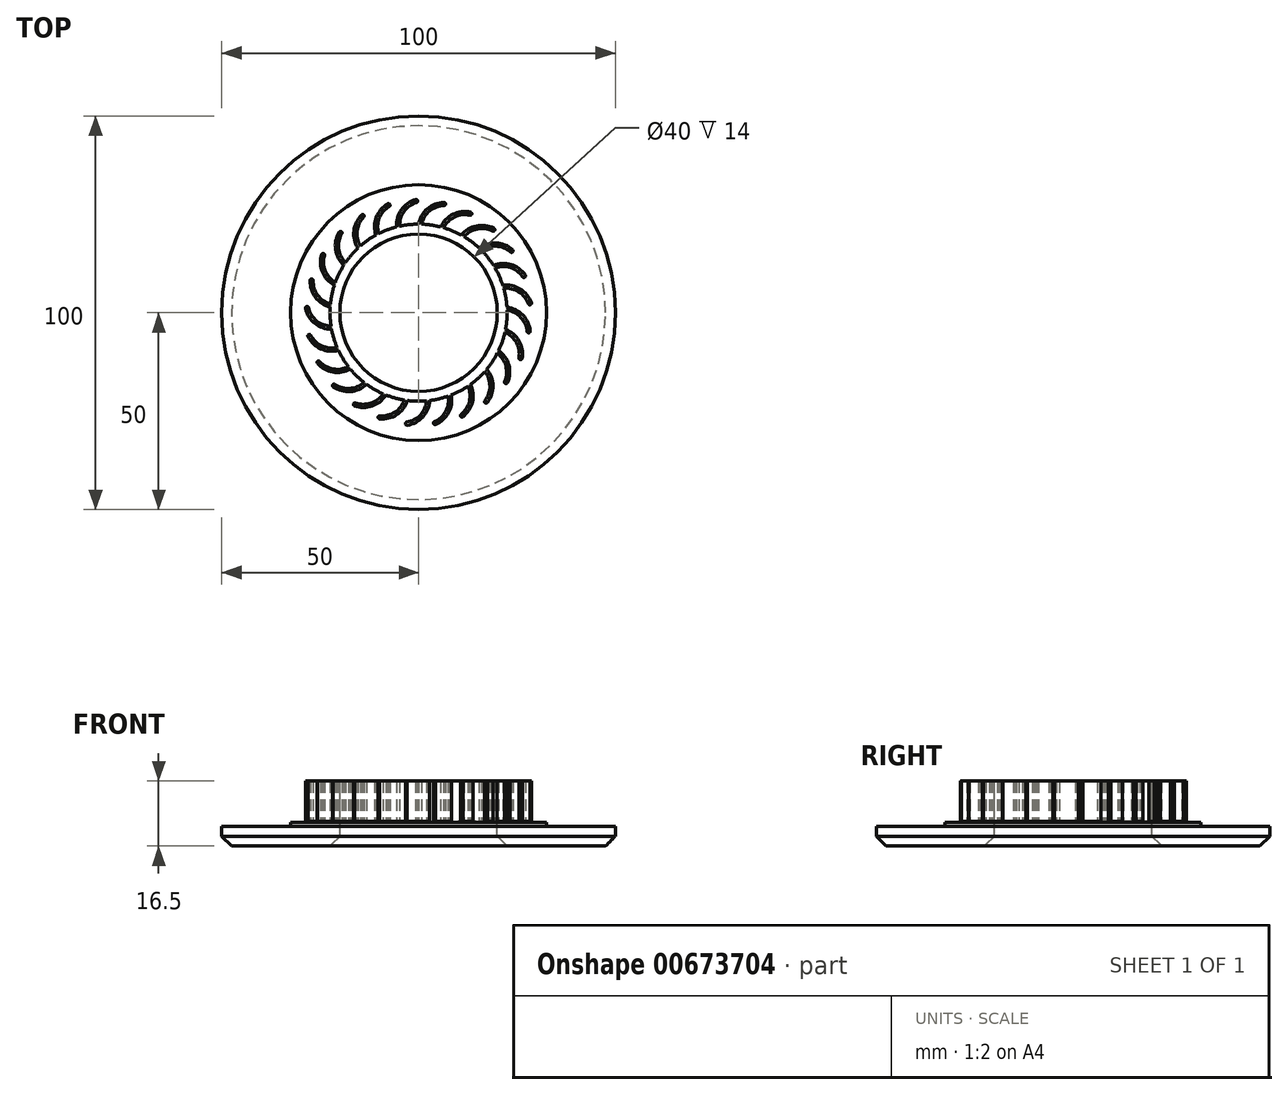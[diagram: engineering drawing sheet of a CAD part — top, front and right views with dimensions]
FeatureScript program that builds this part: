
annotation { "Feature Type Name" : "Feature", "Feature Type Description" : "" }
export const myFeature = defineFeature(function(context is Context, id is Id, definition is map)
    precondition{}
    {
        {
            var Q0;
            Q0=qCreatedBy(makeId("Top.planeOp"),FACE);
            var sketch = newSketch(context, id + "F0", { "sketchPlane" : qUnion([Q0])});
            skCircle(sketch, "E0", {"center": v(0, 0) * mm, "radius": 50 * mm});
            skSolve(sketch);
        }
        {
            var Q0;
            Q0=makeQuery(id+"F0.imprint","IMPRINT",FACE,{"disambiguationData":[TD([[makeQuery(id+"F0.imprint","IMPRINT",EDGE,{"derivedFrom":sQuery(id+"F0.wireOp",EDGE,"E0")}),1.0]])]});
            extrude(context, id + "F1", {"entities" : qUnion([Q0]), "depth" : 5 * mm, "offsetDistance" : 25 * mm});
        }
        {
            var Q0;
            Q0=makeQuery(id+"F1.opExtrude","CAP_FACE",FACE,{"disambiguationData":[OSD([sQuery(id+"F0.wireOp",EDGE,"E0")])],"isStart":false});
            var sketch = newSketch(context, id + "F2", { "sketchPlane" : qUnion([Q0])});
            skCircle(sketch, "E1", {"center": v(0, 0) * mm, "radius": 32.5 * mm});
            skSolve(sketch);
        }
        {
            var Q0;
            Q0=makeQuery(id+"F2.imprint","IMPRINT",FACE,{"disambiguationData":[TD([[makeQuery(id+"F2.imprint","IMPRINT",EDGE,{"derivedFrom":sQuery(id+"F2.wireOp",EDGE,"E1")}),1.0]])]});
            extrude(context, id + "F3", {"entities" : qUnion([Q0]), "operationType" : NewBodyOperationType.ADD, "depth" : 1 * mm, "offsetDistance" : 25 * mm});
        }
        {
            var Q0;
            Q0=makeQuery(id+"F1.opExtrude","CAP_EDGE",EDGE,{"disambiguationData":[OSD([sQuery(id+"F0.wireOp",EDGE,"E0")])],"isStart":true});
            chamfer(context, id + "F4", {"entities" : qUnion([Q0]), "width" : 2.5 * mm, "tangentPropagation" : true});
        }
        {
            var Q0;
            Q0=makeQuery(id+"F3.opExtrude","CAP_FACE",FACE,{"disambiguationData":[OSD([sQuery(id+"F2.wireOp",EDGE,"E1")])],"isStart":false});
            var sketch = newSketch(context, id + "F5", { "sketchPlane" : qUnion([Q0])});
            skCircle(sketch, "E2", {"center": v(0, 0) * mm, "radius": 28.75 * mm});
            skCircle(sketch, "E3", {"center": v(0, 0) * mm, "radius": 22.5 * mm});
            skArc(sketch, "E4", {"start": v(6.45, 28.02) * mm, "mid": v(2.25, 26.4) * mm, "end": v(0, 22.5) * mm});
            skArc(sketch, "E5.0", {"start": v(6.47, 27.22) * mm, "mid": v(2.82, 25.84) * mm, "end": v(0.81, 22.49) * mm});
            skArc(sketch, "E6", {"start": v(6.45, 28.02) * mm, "mid": v(6.86, 27.63) * mm, "end": v(6.47, 27.22) * mm});
            skArc(sketch, "E7.1.0", {"start": v(-0.72, 28.74) * mm, "mid": v(-4.39, 26.13) * mm, "end": v(-5.6, 21.8) * mm});
            skArc(sketch, "E7.1.1", {"start": v(-0.5, 27.97) * mm, "mid": v(-3.7, 25.73) * mm, "end": v(-4.8, 21.98) * mm});
            skArc(sketch, "E7.1.2", {"start": v(-0.72, 28.74) * mm, "mid": v(-0.22, 28.47) * mm, "end": v(-0.5, 27.97) * mm});
            skArc(sketch, "E7.2.0", {"start": v(-7.84, 27.66) * mm, "mid": v(-10.75, 24.22) * mm, "end": v(-10.84, 19.72) * mm});
            skArc(sketch, "E7.2.1", {"start": v(-7.44, 26.97) * mm, "mid": v(-9.98, 24) * mm, "end": v(-10.12, 20.1) * mm});
            skArc(sketch, "E7.2.2", {"start": v(-7.84, 27.66) * mm, "mid": v(-7.3, 27.52) * mm, "end": v(-7.44, 26.97) * mm});
            skArc(sketch, "E7.3.0", {"start": v(-14.47, 24.84) * mm, "mid": v(-16.44, 20.79) * mm, "end": v(-15.4, 16.4) * mm});
            skArc(sketch, "E7.3.1", {"start": v(-13.91, 24.27) * mm, "mid": v(-15.63, 20.76) * mm, "end": v(-14.8, 16.95) * mm});
            skArc(sketch, "E7.3.2", {"start": v(-14.47, 24.84) * mm, "mid": v(-13.9, 24.84) * mm, "end": v(-13.91, 24.27) * mm});
            skArc(sketch, "E7.4.0", {"start": v(-20.2, 20.46) * mm, "mid": v(-21.09, 16.05) * mm, "end": v(-19, 12.06) * mm});
            skArc(sketch, "E7.4.1", {"start": v(-19.51, 20.05) * mm, "mid": v(-20.3, 16.22) * mm, "end": v(-18.55, 12.73) * mm});
            skArc(sketch, "E7.4.2", {"start": v(-20.2, 20.46) * mm, "mid": v(-19.65, 20.6) * mm, "end": v(-19.51, 20.05) * mm});
            skArc(sketch, "E7.5.0", {"start": v(-24.65, 14.8) * mm, "mid": v(-24.42, 10.3) * mm, "end": v(-21.4, 6.95) * mm});
            skArc(sketch, "E7.5.1", {"start": v(-23.88, 14.57) * mm, "mid": v(-23.7, 10.66) * mm, "end": v(-21.13, 7.72) * mm});
            skArc(sketch, "E7.5.2", {"start": v(-24.65, 14.8) * mm, "mid": v(-24.15, 15.06) * mm, "end": v(-23.88, 14.57) * mm});
            skArc(sketch, "E7.6.0", {"start": v(-27.56, 8.2) * mm, "mid": v(-26.2, 3.9) * mm, "end": v(-22.46, 1.41) * mm});
            skArc(sketch, "E7.6.1", {"start": v(-26.76, 8.17) * mm, "mid": v(-25.6, 4.44) * mm, "end": v(-22.39, 2.22) * mm});
            skArc(sketch, "E7.6.2", {"start": v(-27.56, 8.2) * mm, "mid": v(-27.14, 8.58) * mm, "end": v(-26.76, 8.17) * mm});
            skArc(sketch, "E7.7.0", {"start": v(-28.73, 1.09) * mm, "mid": v(-26.36, -2.74) * mm, "end": v(-22.1, -4.22) * mm});
            skArc(sketch, "E7.7.1", {"start": v(-27.95, 1.26) * mm, "mid": v(-25.9, -2.07) * mm, "end": v(-22.24, -3.42) * mm});
            skArc(sketch, "E7.7.2", {"start": v(-28.73, 1.09) * mm, "mid": v(-28.42, 1.57) * mm, "end": v(-27.95, 1.26) * mm});
            skArc(sketch, "E7.8.0", {"start": v(-28.1, -6.09) * mm, "mid": v(-24.85, -9.2) * mm, "end": v(-20.36, -9.58) * mm});
            skArc(sketch, "E7.8.1", {"start": v(-27.38, -5.73) * mm, "mid": v(-24.58, -8.45) * mm, "end": v(-20.7, -8.84) * mm});
            skArc(sketch, "E7.8.2", {"start": v(-28.1, -6.09) * mm, "mid": v(-27.92, -5.55) * mm, "end": v(-27.38, -5.73) * mm});
            skArc(sketch, "E7.9.0", {"start": v(-25.7, -12.89) * mm, "mid": v(-21.78, -15.1) * mm, "end": v(-17.34, -14.34) * mm});
            skArc(sketch, "E7.9.1", {"start": v(-25.1, -12.36) * mm, "mid": v(-21.7, -14.3) * mm, "end": v(-17.84, -13.7) * mm});
            skArc(sketch, "E7.9.2", {"start": v(-25.7, -12.89) * mm, "mid": v(-25.66, -12.32) * mm, "end": v(-25.1, -12.36) * mm});
            skArc(sketch, "E7.10.0", {"start": v(-21.69, -18.87) * mm, "mid": v(-17.34, -20.04) * mm, "end": v(-13.23, -18.2) * mm});
            skArc(sketch, "E7.10.1", {"start": v(-21.24, -18.21) * mm, "mid": v(-17.47, -19.25) * mm, "end": v(-13.87, -17.71) * mm});
            skArc(sketch, "E7.10.2", {"start": v(-21.69, -18.87) * mm, "mid": v(-21.8, -18.32) * mm, "end": v(-21.24, -18.21) * mm});
            skArc(sketch, "E7.11.0", {"start": v(-16.31, -23.67) * mm, "mid": v(-11.8, -23.72) * mm, "end": v(-8.28, -20.92) * mm});
            skArc(sketch, "E7.11.1", {"start": v(-16.04, -22.92) * mm, "mid": v(-12.13, -22.99) * mm, "end": v(-9.03, -20.6) * mm});
            skArc(sketch, "E7.11.2", {"start": v(-16.31, -23.67) * mm, "mid": v(-16.55, -23.16) * mm, "end": v(-16.04, -22.92) * mm});
            skArc(sketch, "E7.12.0", {"start": v(-9.91, -26.99) * mm, "mid": v(-5.54, -25.91) * mm, "end": v(-2.82, -22.32) * mm});
            skArc(sketch, "E7.12.1", {"start": v(-9.83, -26.2) * mm, "mid": v(-6.03, -25.28) * mm, "end": v(-3.62, -22.2) * mm});
            skArc(sketch, "E7.12.2", {"start": v(-9.91, -26.99) * mm, "mid": v(-10.27, -26.55) * mm, "end": v(-9.83, -26.2) * mm});
            skArc(sketch, "E7.13.0", {"start": v(-2.9, -28.6) * mm, "mid": v(1.08, -26.48) * mm, "end": v(2.82, -22.32) * mm});
            skArc(sketch, "E7.13.1", {"start": v(-3.01, -27.81) * mm, "mid": v(0.44, -25.99) * mm, "end": v(2.01, -22.4) * mm});
            skArc(sketch, "E7.13.2", {"start": v(-2.9, -28.6) * mm, "mid": v(-3.35, -28.27) * mm, "end": v(-3.01, -27.81) * mm});
            skArc(sketch, "E7.14.0", {"start": v(4.31, -28.42) * mm, "mid": v(7.63, -25.38) * mm, "end": v(8.28, -20.92) * mm});
            skArc(sketch, "E7.14.1", {"start": v(4, -27.69) * mm, "mid": v(6.9, -25.06) * mm, "end": v(7.52, -21.2) * mm});
            skArc(sketch, "E7.14.2", {"start": v(4.31, -28.42) * mm, "mid": v(3.79, -28.21) * mm, "end": v(4, -27.69) * mm});
            skArc(sketch, "E7.15.0", {"start": v(11.25, -26.46) * mm, "mid": v(13.7, -22.68) * mm, "end": v(13.23, -18.2) * mm});
            skArc(sketch, "E7.15.1", {"start": v(10.76, -25.82) * mm, "mid": v(12.9, -22.56) * mm, "end": v(12.56, -18.67) * mm});
            skArc(sketch, "E7.15.2", {"start": v(11.25, -26.46) * mm, "mid": v(10.69, -26.38) * mm, "end": v(10.76, -25.82) * mm});
            skArc(sketch, "E7.16.0", {"start": v(17.47, -22.83) * mm, "mid": v(18.91, -18.56) * mm, "end": v(17.34, -14.34) * mm});
            skArc(sketch, "E7.16.1", {"start": v(16.84, -22.34) * mm, "mid": v(18.11, -18.64) * mm, "end": v(16.8, -14.96) * mm});
            skArc(sketch, "E7.16.2", {"start": v(17.47, -22.83) * mm, "mid": v(16.91, -22.9) * mm, "end": v(16.84, -22.34) * mm});
            skArc(sketch, "E7.17.0", {"start": v(22.6, -17.77) * mm, "mid": v(22.93, -13.28) * mm, "end": v(20.36, -9.58) * mm});
            skArc(sketch, "E7.17.1", {"start": v(21.87, -17.45) * mm, "mid": v(22.18, -13.55) * mm, "end": v(20, -10.3) * mm});
            skArc(sketch, "E7.17.2", {"start": v(22.6, -17.77) * mm, "mid": v(22.07, -17.97) * mm, "end": v(21.87, -17.45) * mm});
            skArc(sketch, "E7.18.0", {"start": v(26.31, -11.59) * mm, "mid": v(25.51, -7.16) * mm, "end": v(22.1, -4.22) * mm});
            skArc(sketch, "E7.18.1", {"start": v(25.52, -11.46) * mm, "mid": v(24.85, -7.61) * mm, "end": v(21.93, -5.01) * mm});
            skArc(sketch, "E7.18.2", {"start": v(26.31, -11.59) * mm, "mid": v(25.85, -11.92) * mm, "end": v(25.52, -11.46) * mm});
            skArc(sketch, "E7.19.0", {"start": v(28.37, -4.68) * mm, "mid": v(26.5, -0.59) * mm, "end": v(22.46, 1.41) * mm});
            skArc(sketch, "E7.19.1", {"start": v(27.57, -4.75) * mm, "mid": v(25.96, -1.2) * mm, "end": v(22.5, 0.6) * mm});
            skArc(sketch, "E7.19.2", {"start": v(28.37, -4.68) * mm, "mid": v(28, -5.12) * mm, "end": v(27.57, -4.75) * mm});
            skArc(sketch, "E7.20.0", {"start": v(28.64, 2.52) * mm, "mid": v(25.8, 6.02) * mm, "end": v(21.4, 6.95) * mm});
            skArc(sketch, "E7.20.1", {"start": v(27.89, 2.25) * mm, "mid": v(25.44, 5.3) * mm, "end": v(21.64, 6.18) * mm});
            skArc(sketch, "E7.20.2", {"start": v(28.64, 2.52) * mm, "mid": v(28.4, 2) * mm, "end": v(27.89, 2.25) * mm});
            skArc(sketch, "E7.21.0", {"start": v(27.11, 9.56) * mm, "mid": v(23.5, 12.25) * mm, "end": v(19, 12.06) * mm});
            skArc(sketch, "E7.21.1", {"start": v(26.45, 9.12) * mm, "mid": v(23.33, 11.46) * mm, "end": v(19.42, 11.36) * mm});
            skArc(sketch, "E7.21.2", {"start": v(27.11, 9.56) * mm, "mid": v(27, 9) * mm, "end": v(26.45, 9.12) * mm});
            skArc(sketch, "E7.22.0", {"start": v(23.88, 16) * mm, "mid": v(19.71, 17.7) * mm, "end": v(15.4, 16.4) * mm});
            skArc(sketch, "E7.22.1", {"start": v(23.35, 15.4) * mm, "mid": v(19.74, 16.9) * mm, "end": v(15.98, 15.84) * mm});
            skArc(sketch, "E7.22.2", {"start": v(23.88, 16) * mm, "mid": v(23.92, 15.44) * mm, "end": v(23.35, 15.4) * mm});
            skArc(sketch, "E7.23.0", {"start": v(19.15, 21.44) * mm, "mid": v(14.69, 22.05) * mm, "end": v(10.84, 19.72) * mm});
            skArc(sketch, "E7.23.1", {"start": v(18.78, 20.73) * mm, "mid": v(14.92, 21.28) * mm, "end": v(11.54, 19.31) * mm});
            skArc(sketch, "E7.23.2", {"start": v(19.15, 21.44) * mm, "mid": v(19.32, 20.9) * mm, "end": v(18.78, 20.73) * mm});
            skArc(sketch, "E7.24.0", {"start": v(13.22, 25.53) * mm, "mid": v(8.74, 25.01) * mm, "end": v(5.6, 21.8) * mm});
            skArc(sketch, "E7.24.1", {"start": v(13.04, 24.75) * mm, "mid": v(9.16, 24.33) * mm, "end": v(6.38, 21.58) * mm});
            skArc(sketch, "E7.24.2", {"start": v(13.22, 25.53) * mm, "mid": v(13.52, 25.05) * mm, "end": v(13.04, 24.75) * mm});
            skSolve(sketch);
        }
        {
            var Q0;
            {var subQ0=sQuery(id+"F5.wireOp",EDGE,"E3");var subQ33=makeQuery(id+"F5.imprint","INTERSECT",VERTEX,{"derivedFrom":[subQ0,sQuery(id+"F5.wireOp",EDGE,"E7.19.0")]});Q0=makeQuery(id+"F5.imprint","IMPRINT",FACE,{"disambiguationData":[TD([[makeQuery(id+"F5.imprint","IMPRINT",EDGE,{"disambiguationData":[TD([[subQ33,1.0]])],"derivedFrom":subQ0}),1.0]])]});}
            var Q1;
            {var subQ0=sQuery(id+"F5.wireOp",EDGE,"E7.3.0");Q1=makeQuery(id+"F5.imprint","IMPRINT",FACE,{"disambiguationData":[TD([[makeQuery(id+"F5.imprint","IMPRINT",EDGE,{"derivedFrom":subQ0}),1.0]])]});}
            var Q2;
            {var subQ0=sQuery(id+"F5.wireOp",EDGE,"E7.2.0");Q2=makeQuery(id+"F5.imprint","IMPRINT",FACE,{"disambiguationData":[TD([[makeQuery(id+"F5.imprint","IMPRINT",EDGE,{"derivedFrom":subQ0}),1.0]])]});}
            var Q3;
            {var subQ1=sQuery(id+"F5.wireOp",EDGE,"E7.1.0");Q3=makeQuery(id+"F5.imprint","IMPRINT",FACE,{"disambiguationData":[TD([[makeQuery(id+"F5.imprint","IMPRINT",EDGE,{"derivedFrom":subQ1}),1.0]])]});}
            var Q4;
            {var subQ1=sQuery(id+"F5.wireOp",EDGE,"E4");Q4=makeQuery(id+"F5.imprint","IMPRINT",FACE,{"disambiguationData":[TD([[makeQuery(id+"F5.imprint","IMPRINT",EDGE,{"derivedFrom":subQ1}),1.0]])]});}
            var Q5;
            {var subQ1=sQuery(id+"F5.wireOp",EDGE,"E7.24.0");Q5=makeQuery(id+"F5.imprint","IMPRINT",FACE,{"disambiguationData":[TD([[makeQuery(id+"F5.imprint","IMPRINT",EDGE,{"derivedFrom":subQ1}),1.0]])]});}
            var Q6;
            {var subQ0=sQuery(id+"F5.wireOp",EDGE,"E7.23.0");Q6=makeQuery(id+"F5.imprint","IMPRINT",FACE,{"disambiguationData":[TD([[makeQuery(id+"F5.imprint","IMPRINT",EDGE,{"derivedFrom":subQ0}),1.0]])]});}
            var Q7;
            {var subQ0=sQuery(id+"F5.wireOp",EDGE,"E7.22.0");Q7=makeQuery(id+"F5.imprint","IMPRINT",FACE,{"disambiguationData":[TD([[makeQuery(id+"F5.imprint","IMPRINT",EDGE,{"derivedFrom":subQ0}),1.0]])]});}
            var Q8;
            {var subQ1=sQuery(id+"F5.wireOp",EDGE,"E7.21.0");Q8=makeQuery(id+"F5.imprint","IMPRINT",FACE,{"disambiguationData":[TD([[makeQuery(id+"F5.imprint","IMPRINT",EDGE,{"derivedFrom":subQ1}),1.0]])]});}
            var Q9;
            {var subQ1=sQuery(id+"F5.wireOp",EDGE,"E7.20.0");Q9=makeQuery(id+"F5.imprint","IMPRINT",FACE,{"disambiguationData":[TD([[makeQuery(id+"F5.imprint","IMPRINT",EDGE,{"derivedFrom":subQ1}),1.0]])]});}
            var Q10;
            {var subQ1=sQuery(id+"F5.wireOp",EDGE,"E7.19.0");Q10=makeQuery(id+"F5.imprint","IMPRINT",FACE,{"disambiguationData":[TD([[makeQuery(id+"F5.imprint","IMPRINT",EDGE,{"derivedFrom":subQ1}),1.0]])]});}
            var Q11;
            {var subQ0=sQuery(id+"F5.wireOp",EDGE,"E7.18.0");Q11=makeQuery(id+"F5.imprint","IMPRINT",FACE,{"disambiguationData":[TD([[makeQuery(id+"F5.imprint","IMPRINT",EDGE,{"derivedFrom":subQ0}),1.0]])]});}
            var Q12;
            {var subQ0=sQuery(id+"F5.wireOp",EDGE,"E7.17.0");Q12=makeQuery(id+"F5.imprint","IMPRINT",FACE,{"disambiguationData":[TD([[makeQuery(id+"F5.imprint","IMPRINT",EDGE,{"derivedFrom":subQ0}),1.0]])]});}
            var Q13;
            {var subQ1=sQuery(id+"F5.wireOp",EDGE,"E7.16.0");Q13=makeQuery(id+"F5.imprint","IMPRINT",FACE,{"disambiguationData":[TD([[makeQuery(id+"F5.imprint","IMPRINT",EDGE,{"derivedFrom":subQ1}),1.0]])]});}
            var Q14;
            {var subQ2=sQuery(id+"F5.wireOp",EDGE,"E7.15.0");Q14=makeQuery(id+"F5.imprint","IMPRINT",FACE,{"disambiguationData":[TD([[makeQuery(id+"F5.imprint","IMPRINT",EDGE,{"derivedFrom":subQ2}),1.0]])]});}
            var Q15;
            {var subQ1=sQuery(id+"F5.wireOp",EDGE,"E7.14.0");Q15=makeQuery(id+"F5.imprint","IMPRINT",FACE,{"disambiguationData":[TD([[makeQuery(id+"F5.imprint","IMPRINT",EDGE,{"derivedFrom":subQ1}),1.0]])]});}
            var Q16;
            {var subQ0=sQuery(id+"F5.wireOp",EDGE,"E7.13.0");Q16=makeQuery(id+"F5.imprint","IMPRINT",FACE,{"disambiguationData":[TD([[makeQuery(id+"F5.imprint","IMPRINT",EDGE,{"derivedFrom":subQ0}),1.0]])]});}
            var Q17;
            {var subQ0=sQuery(id+"F5.wireOp",EDGE,"E7.12.0");Q17=makeQuery(id+"F5.imprint","IMPRINT",FACE,{"disambiguationData":[TD([[makeQuery(id+"F5.imprint","IMPRINT",EDGE,{"derivedFrom":subQ0}),1.0]])]});}
            var Q18;
            {var subQ1=sQuery(id+"F5.wireOp",EDGE,"E7.11.0");Q18=makeQuery(id+"F5.imprint","IMPRINT",FACE,{"disambiguationData":[TD([[makeQuery(id+"F5.imprint","IMPRINT",EDGE,{"derivedFrom":subQ1}),1.0]])]});}
            var Q19;
            {var subQ1=sQuery(id+"F5.wireOp",EDGE,"E7.10.0");Q19=makeQuery(id+"F5.imprint","IMPRINT",FACE,{"disambiguationData":[TD([[makeQuery(id+"F5.imprint","IMPRINT",EDGE,{"derivedFrom":subQ1}),1.0]])]});}
            var Q20;
            {var subQ1=sQuery(id+"F5.wireOp",EDGE,"E7.9.0");Q20=makeQuery(id+"F5.imprint","IMPRINT",FACE,{"disambiguationData":[TD([[makeQuery(id+"F5.imprint","IMPRINT",EDGE,{"derivedFrom":subQ1}),1.0]])]});}
            var Q21;
            {var subQ0=sQuery(id+"F5.wireOp",EDGE,"E7.8.0");Q21=makeQuery(id+"F5.imprint","IMPRINT",FACE,{"disambiguationData":[TD([[makeQuery(id+"F5.imprint","IMPRINT",EDGE,{"derivedFrom":subQ0}),1.0]])]});}
            var Q22;
            {var subQ0=sQuery(id+"F5.wireOp",EDGE,"E7.7.0");Q22=makeQuery(id+"F5.imprint","IMPRINT",FACE,{"disambiguationData":[TD([[makeQuery(id+"F5.imprint","IMPRINT",EDGE,{"derivedFrom":subQ0}),1.0]])]});}
            var Q23;
            {var subQ1=sQuery(id+"F5.wireOp",EDGE,"E7.6.0");Q23=makeQuery(id+"F5.imprint","IMPRINT",FACE,{"disambiguationData":[TD([[makeQuery(id+"F5.imprint","IMPRINT",EDGE,{"derivedFrom":subQ1}),1.0]])]});}
            var Q24;
            {var subQ1=sQuery(id+"F5.wireOp",EDGE,"E7.5.0");Q24=makeQuery(id+"F5.imprint","IMPRINT",FACE,{"disambiguationData":[TD([[makeQuery(id+"F5.imprint","IMPRINT",EDGE,{"derivedFrom":subQ1}),1.0]])]});}
            var Q25;
            {var subQ2=sQuery(id+"F5.wireOp",EDGE,"E7.4.0");Q25=makeQuery(id+"F5.imprint","IMPRINT",FACE,{"disambiguationData":[TD([[makeQuery(id+"F5.imprint","IMPRINT",EDGE,{"derivedFrom":subQ2}),1.0]])]});}
            extrude(context, id + "F6", {"entities" : qUnion([Q0, Q1, Q2, Q3, Q4, Q5, Q6, Q7, Q8, Q9, Q10, Q11, Q12, Q13, Q14, Q15, Q16, Q17, Q18, Q19, Q20, Q21, Q22, Q23, Q24, Q25]), "operationType" : NewBodyOperationType.ADD, "depth" : 10.5 * mm, "offsetDistance" : 25 * mm});
        }
        {
            var Q0;
            {var subQ0=sQuery(id+"F5.wireOp",EDGE,"E7.12.0");Q0=makeQuery(id+"F5.imprint","IMPRINT",FACE,{"disambiguationData":[TD([[makeQuery(id+"F5.imprint","IMPRINT",EDGE,{"derivedFrom":subQ0}),1.0]])]});}
            var Q1;
            {var subQ1=sQuery(id+"F5.wireOp",EDGE,"E7.11.0");Q1=makeQuery(id+"F5.imprint","IMPRINT",FACE,{"disambiguationData":[TD([[makeQuery(id+"F5.imprint","IMPRINT",EDGE,{"derivedFrom":subQ1}),1.0]])]});}
            var Q2;
            {var subQ1=sQuery(id+"F5.wireOp",EDGE,"E7.10.0");Q2=makeQuery(id+"F5.imprint","IMPRINT",FACE,{"disambiguationData":[TD([[makeQuery(id+"F5.imprint","IMPRINT",EDGE,{"derivedFrom":subQ1}),1.0]])]});}
            var Q3;
            {var subQ1=sQuery(id+"F5.wireOp",EDGE,"E7.9.0");Q3=makeQuery(id+"F5.imprint","IMPRINT",FACE,{"disambiguationData":[TD([[makeQuery(id+"F5.imprint","IMPRINT",EDGE,{"derivedFrom":subQ1}),1.0]])]});}
            var Q4;
            {var subQ0=sQuery(id+"F5.wireOp",EDGE,"E7.8.0");Q4=makeQuery(id+"F5.imprint","IMPRINT",FACE,{"disambiguationData":[TD([[makeQuery(id+"F5.imprint","IMPRINT",EDGE,{"derivedFrom":subQ0}),1.0]])]});}
            var Q5;
            {var subQ0=sQuery(id+"F5.wireOp",EDGE,"E7.7.0");Q5=makeQuery(id+"F5.imprint","IMPRINT",FACE,{"disambiguationData":[TD([[makeQuery(id+"F5.imprint","IMPRINT",EDGE,{"derivedFrom":subQ0}),1.0]])]});}
            var Q6;
            {var subQ1=sQuery(id+"F5.wireOp",EDGE,"E7.6.0");Q6=makeQuery(id+"F5.imprint","IMPRINT",FACE,{"disambiguationData":[TD([[makeQuery(id+"F5.imprint","IMPRINT",EDGE,{"derivedFrom":subQ1}),1.0]])]});}
            var Q7;
            {var subQ1=sQuery(id+"F5.wireOp",EDGE,"E7.5.0");Q7=makeQuery(id+"F5.imprint","IMPRINT",FACE,{"disambiguationData":[TD([[makeQuery(id+"F5.imprint","IMPRINT",EDGE,{"derivedFrom":subQ1}),1.0]])]});}
            var Q8;
            {var subQ2=sQuery(id+"F5.wireOp",EDGE,"E7.4.0");Q8=makeQuery(id+"F5.imprint","IMPRINT",FACE,{"disambiguationData":[TD([[makeQuery(id+"F5.imprint","IMPRINT",EDGE,{"derivedFrom":subQ2}),1.0]])]});}
            var Q9;
            {var subQ0=sQuery(id+"F5.wireOp",EDGE,"E7.3.0");Q9=makeQuery(id+"F5.imprint","IMPRINT",FACE,{"disambiguationData":[TD([[makeQuery(id+"F5.imprint","IMPRINT",EDGE,{"derivedFrom":subQ0}),1.0]])]});}
            var Q10;
            {var subQ0=sQuery(id+"F5.wireOp",EDGE,"E7.2.0");Q10=makeQuery(id+"F5.imprint","IMPRINT",FACE,{"disambiguationData":[TD([[makeQuery(id+"F5.imprint","IMPRINT",EDGE,{"derivedFrom":subQ0}),1.0]])]});}
            var Q11;
            {var subQ1=sQuery(id+"F5.wireOp",EDGE,"E7.1.0");Q11=makeQuery(id+"F5.imprint","IMPRINT",FACE,{"disambiguationData":[TD([[makeQuery(id+"F5.imprint","IMPRINT",EDGE,{"derivedFrom":subQ1}),1.0]])]});}
            var Q12;
            {var subQ1=sQuery(id+"F5.wireOp",EDGE,"E4");Q12=makeQuery(id+"F5.imprint","IMPRINT",FACE,{"disambiguationData":[TD([[makeQuery(id+"F5.imprint","IMPRINT",EDGE,{"derivedFrom":subQ1}),1.0]])]});}
            var Q13;
            {var subQ1=sQuery(id+"F5.wireOp",EDGE,"E7.24.0");Q13=makeQuery(id+"F5.imprint","IMPRINT",FACE,{"disambiguationData":[TD([[makeQuery(id+"F5.imprint","IMPRINT",EDGE,{"derivedFrom":subQ1}),1.0]])]});}
            var Q14;
            {var subQ0=sQuery(id+"F5.wireOp",EDGE,"E7.23.0");Q14=makeQuery(id+"F5.imprint","IMPRINT",FACE,{"disambiguationData":[TD([[makeQuery(id+"F5.imprint","IMPRINT",EDGE,{"derivedFrom":subQ0}),1.0]])]});}
            var Q15;
            {var subQ0=sQuery(id+"F5.wireOp",EDGE,"E7.22.0");Q15=makeQuery(id+"F5.imprint","IMPRINT",FACE,{"disambiguationData":[TD([[makeQuery(id+"F5.imprint","IMPRINT",EDGE,{"derivedFrom":subQ0}),1.0]])]});}
            var Q16;
            {var subQ1=sQuery(id+"F5.wireOp",EDGE,"E7.21.0");Q16=makeQuery(id+"F5.imprint","IMPRINT",FACE,{"disambiguationData":[TD([[makeQuery(id+"F5.imprint","IMPRINT",EDGE,{"derivedFrom":subQ1}),1.0]])]});}
            var Q17;
            {var subQ1=sQuery(id+"F5.wireOp",EDGE,"E7.20.0");Q17=makeQuery(id+"F5.imprint","IMPRINT",FACE,{"disambiguationData":[TD([[makeQuery(id+"F5.imprint","IMPRINT",EDGE,{"derivedFrom":subQ1}),1.0]])]});}
            var Q18;
            {var subQ1=sQuery(id+"F5.wireOp",EDGE,"E7.19.0");Q18=makeQuery(id+"F5.imprint","IMPRINT",FACE,{"disambiguationData":[TD([[makeQuery(id+"F5.imprint","IMPRINT",EDGE,{"derivedFrom":subQ1}),1.0]])]});}
            var Q19;
            {var subQ0=sQuery(id+"F5.wireOp",EDGE,"E7.18.0");Q19=makeQuery(id+"F5.imprint","IMPRINT",FACE,{"disambiguationData":[TD([[makeQuery(id+"F5.imprint","IMPRINT",EDGE,{"derivedFrom":subQ0}),1.0]])]});}
            var Q20;
            {var subQ0=sQuery(id+"F5.wireOp",EDGE,"E7.17.0");Q20=makeQuery(id+"F5.imprint","IMPRINT",FACE,{"disambiguationData":[TD([[makeQuery(id+"F5.imprint","IMPRINT",EDGE,{"derivedFrom":subQ0}),1.0]])]});}
            var Q21;
            {var subQ1=sQuery(id+"F5.wireOp",EDGE,"E7.16.0");Q21=makeQuery(id+"F5.imprint","IMPRINT",FACE,{"disambiguationData":[TD([[makeQuery(id+"F5.imprint","IMPRINT",EDGE,{"derivedFrom":subQ1}),1.0]])]});}
            var Q22;
            {var subQ2=sQuery(id+"F5.wireOp",EDGE,"E7.15.0");Q22=makeQuery(id+"F5.imprint","IMPRINT",FACE,{"disambiguationData":[TD([[makeQuery(id+"F5.imprint","IMPRINT",EDGE,{"derivedFrom":subQ2}),1.0]])]});}
            var Q23;
            {var subQ1=sQuery(id+"F5.wireOp",EDGE,"E7.14.0");Q23=makeQuery(id+"F5.imprint","IMPRINT",FACE,{"disambiguationData":[TD([[makeQuery(id+"F5.imprint","IMPRINT",EDGE,{"derivedFrom":subQ1}),1.0]])]});}
            var Q24;
            {var subQ0=sQuery(id+"F5.wireOp",EDGE,"E7.13.0");Q24=makeQuery(id+"F5.imprint","IMPRINT",FACE,{"disambiguationData":[TD([[makeQuery(id+"F5.imprint","IMPRINT",EDGE,{"derivedFrom":subQ0}),1.0]])]});}
            extrude(context, id + "F7", {"entities" : qUnion([Q0, Q1, Q2, Q3, Q4, Q5, Q6, Q7, Q8, Q9, Q10, Q11, Q12, Q13, Q14, Q15, Q16, Q17, Q18, Q19, Q20, Q21, Q22, Q23, Q24]), "operationType" : NewBodyOperationType.REMOVE, "depth" : 0.2 * mm, "offsetDistance" : 25 * mm});
        }
        {
            var Q0;
            Q0=makeQuery(id+"F6.opExtrude","CAP_FACE",FACE,{"disambiguationData":[OSD([sQuery(id+"F5.wireOp",EDGE,"E2"),sQuery(id+"F5.wireOp",EDGE,"E3"),sQuery(id+"F5.wireOp",EDGE,"ykxsR3wm-vLNf-CyqG-FdRr-AU9aHAGR8XtX"),sQuery(id+"F5.wireOp",EDGE,"7fe3ce4f-9b0d-447d-bd8f-ed196f01170a.0"),sQuery(id+"F5.wireOp",EDGE,"5778bfb5-43b9-4e5e-a337-4516f5bf2484"),sQuery(id+"F5.wireOp",EDGE,"5eb93d57-8787-4972-98d3-99d79eb88372.1.0"),sQuery(id+"F5.wireOp",EDGE,"5eb93d57-8787-4972-98d3-99d79eb88372.1.1"),sQuery(id+"F5.wireOp",EDGE,"5eb93d57-8787-4972-98d3-99d79eb88372.1.2"),sQuery(id+"F5.wireOp",EDGE,"5eb93d57-8787-4972-98d3-99d79eb88372.2.0"),sQuery(id+"F5.wireOp",EDGE,"5eb93d57-8787-4972-98d3-99d79eb88372.2.1"),sQuery(id+"F5.wireOp",EDGE,"5eb93d57-8787-4972-98d3-99d79eb88372.2.2"),sQuery(id+"F5.wireOp",EDGE,"5eb93d57-8787-4972-98d3-99d79eb88372.3.0"),sQuery(id+"F5.wireOp",EDGE,"5eb93d57-8787-4972-98d3-99d79eb88372.3.1"),sQuery(id+"F5.wireOp",EDGE,"5eb93d57-8787-4972-98d3-99d79eb88372.3.2"),sQuery(id+"F5.wireOp",EDGE,"5eb93d57-8787-4972-98d3-99d79eb88372.4.0"),sQuery(id+"F5.wireOp",EDGE,"5eb93d57-8787-4972-98d3-99d79eb88372.4.1"),sQuery(id+"F5.wireOp",EDGE,"5eb93d57-8787-4972-98d3-99d79eb88372.4.2"),sQuery(id+"F5.wireOp",EDGE,"5eb93d57-8787-4972-98d3-99d79eb88372.5.0"),sQuery(id+"F5.wireOp",EDGE,"5eb93d57-8787-4972-98d3-99d79eb88372.5.1"),sQuery(id+"F5.wireOp",EDGE,"5eb93d57-8787-4972-98d3-99d79eb88372.5.2"),sQuery(id+"F5.wireOp",EDGE,"5eb93d57-8787-4972-98d3-99d79eb88372.6.0"),sQuery(id+"F5.wireOp",EDGE,"5eb93d57-8787-4972-98d3-99d79eb88372.6.1"),sQuery(id+"F5.wireOp",EDGE,"5eb93d57-8787-4972-98d3-99d79eb88372.6.2"),sQuery(id+"F5.wireOp",EDGE,"5eb93d57-8787-4972-98d3-99d79eb88372.7.0"),sQuery(id+"F5.wireOp",EDGE,"5eb93d57-8787-4972-98d3-99d79eb88372.7.1"),sQuery(id+"F5.wireOp",EDGE,"5eb93d57-8787-4972-98d3-99d79eb88372.7.2"),sQuery(id+"F5.wireOp",EDGE,"5eb93d57-8787-4972-98d3-99d79eb88372.8.0"),sQuery(id+"F5.wireOp",EDGE,"5eb93d57-8787-4972-98d3-99d79eb88372.8.1"),sQuery(id+"F5.wireOp",EDGE,"5eb93d57-8787-4972-98d3-99d79eb88372.8.2"),sQuery(id+"F5.wireOp",EDGE,"5eb93d57-8787-4972-98d3-99d79eb88372.9.0"),sQuery(id+"F5.wireOp",EDGE,"5eb93d57-8787-4972-98d3-99d79eb88372.9.1"),sQuery(id+"F5.wireOp",EDGE,"5eb93d57-8787-4972-98d3-99d79eb88372.9.2"),sQuery(id+"F5.wireOp",EDGE,"5eb93d57-8787-4972-98d3-99d79eb88372.10.0"),sQuery(id+"F5.wireOp",EDGE,"5eb93d57-8787-4972-98d3-99d79eb88372.10.1"),sQuery(id+"F5.wireOp",EDGE,"5eb93d57-8787-4972-98d3-99d79eb88372.10.2"),sQuery(id+"F5.wireOp",EDGE,"5eb93d57-8787-4972-98d3-99d79eb88372.11.0"),sQuery(id+"F5.wireOp",EDGE,"5eb93d57-8787-4972-98d3-99d79eb88372.11.1"),sQuery(id+"F5.wireOp",EDGE,"5eb93d57-8787-4972-98d3-99d79eb88372.11.2"),sQuery(id+"F5.wireOp",EDGE,"5eb93d57-8787-4972-98d3-99d79eb88372.12.0"),sQuery(id+"F5.wireOp",EDGE,"5eb93d57-8787-4972-98d3-99d79eb88372.12.1"),sQuery(id+"F5.wireOp",EDGE,"5eb93d57-8787-4972-98d3-99d79eb88372.12.2"),sQuery(id+"F5.wireOp",EDGE,"5eb93d57-8787-4972-98d3-99d79eb88372.13.0"),sQuery(id+"F5.wireOp",EDGE,"5eb93d57-8787-4972-98d3-99d79eb88372.13.1"),sQuery(id+"F5.wireOp",EDGE,"5eb93d57-8787-4972-98d3-99d79eb88372.13.2"),sQuery(id+"F5.wireOp",EDGE,"5eb93d57-8787-4972-98d3-99d79eb88372.14.0"),sQuery(id+"F5.wireOp",EDGE,"5eb93d57-8787-4972-98d3-99d79eb88372.14.1"),sQuery(id+"F5.wireOp",EDGE,"5eb93d57-8787-4972-98d3-99d79eb88372.14.2"),sQuery(id+"F5.wireOp",EDGE,"5eb93d57-8787-4972-98d3-99d79eb88372.15.0"),sQuery(id+"F5.wireOp",EDGE,"5eb93d57-8787-4972-98d3-99d79eb88372.15.1"),sQuery(id+"F5.wireOp",EDGE,"5eb93d57-8787-4972-98d3-99d79eb88372.15.2"),sQuery(id+"F5.wireOp",EDGE,"5eb93d57-8787-4972-98d3-99d79eb88372.16.0"),sQuery(id+"F5.wireOp",EDGE,"5eb93d57-8787-4972-98d3-99d79eb88372.16.1"),sQuery(id+"F5.wireOp",EDGE,"5eb93d57-8787-4972-98d3-99d79eb88372.16.2"),sQuery(id+"F5.wireOp",EDGE,"5eb93d57-8787-4972-98d3-99d79eb88372.17.0"),sQuery(id+"F5.wireOp",EDGE,"5eb93d57-8787-4972-98d3-99d79eb88372.17.1"),sQuery(id+"F5.wireOp",EDGE,"5eb93d57-8787-4972-98d3-99d79eb88372.17.2"),sQuery(id+"F5.wireOp",EDGE,"5eb93d57-8787-4972-98d3-99d79eb88372.18.0"),sQuery(id+"F5.wireOp",EDGE,"5eb93d57-8787-4972-98d3-99d79eb88372.18.1"),sQuery(id+"F5.wireOp",EDGE,"5eb93d57-8787-4972-98d3-99d79eb88372.18.2"),sQuery(id+"F5.wireOp",EDGE,"5eb93d57-8787-4972-98d3-99d79eb88372.19.0"),sQuery(id+"F5.wireOp",EDGE,"5eb93d57-8787-4972-98d3-99d79eb88372.19.1"),sQuery(id+"F5.wireOp",EDGE,"5eb93d57-8787-4972-98d3-99d79eb88372.19.2")])],"isStart":false});
            var sketch = newSketch(context, id + "F8", { "sketchPlane" : qUnion([Q0])});
            skCircle(sketch, "E8", {"center": v(0, 0) * mm, "radius": 20 * mm});
            skSolve(sketch);
        }
        {
            var Q0;
            Q0=makeQuery(id+"F8.imprint","IMPRINT",FACE,{"disambiguationData":[TD([[makeQuery(id+"F8.imprint","IMPRINT",EDGE,{"derivedFrom":sQuery(id+"F8.wireOp",EDGE,"E8")}),1.0]])]});
            extrude(context, id + "F9", {"entities" : qUnion([Q0]), "operationType" : NewBodyOperationType.REMOVE, "endBound" : BoundingType.THROUGH_ALL, "oppositeDirection" : true, "depth" : 25 * mm, "offsetDistance" : 25 * mm});
        }
        {
            var Q0;
            Q0=makeQuery(id+"F9.boolean.opBoolean","INTERSECT",EDGE,{"derivedFrom":[makeQuery(id+"F1.opExtrude","CAP_FACE",FACE,{"disambiguationData":[OSD([sQuery(id+"F0.wireOp",EDGE,"E0")])],"isStart":true}),makeQuery(id+"F9.opExtrude","SWEPT_FACE",FACE,{"disambiguationData":[OSD([sQuery(id+"F8.wireOp",EDGE,"E8")])]})]});
            chamfer(context, id + "F10", {"entities" : qUnion([Q0]), "width" : 2.5 * mm, "tangentPropagation" : true});
        }
    });
